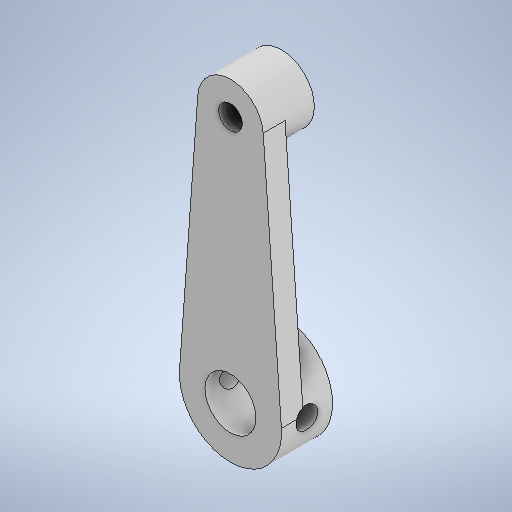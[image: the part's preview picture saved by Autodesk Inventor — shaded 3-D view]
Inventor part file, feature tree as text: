
AUTODESK INVENTOR PART (.ipt)
format: ipt  version: 2025.1 (Build 291241000, 241)  size: 302,080 bytes
history: native  units: mm
features: sketch x4, hole x3, extrude x2, plane x1
ambient origin geometry x8: Origin, YZ Plane, XZ Plane, XY Plane, X Axis, Y Axis, Z Axis, Center Point
bodies: Volumenkörper1 (feature_tree)
feature tree (10):
  extrude  "Extrusion1"  Depth=14.0mm
  extrude  "Extrusion2"  Depth=3.0mm TaperAngle=0.0deg
  sketch  "Skizze3"  dims[d5=9.0mm d6=14.0mm]
  hole  "Bohrung1"  [1 undecoded]
  hole  "Bohrung2"  [1 undecoded]
  plane  "Arbeitsebene1"
  hole  "Bohrung3"  [1 undecoded]
  sketch  "Skizze1"  dims[d0=34.0mm d1=14.0mm]
  sketch  "Skizze2"  dims[d2=9.0mm d3=3.0mm d4=0.0mm]
  sketch  "Skizze4"  dims[d7=4.0mm d8=0.0mm d9=3.242mm d10=8.0mm d11=4.0mm d12=2.0mm d13=90.0deg d14=11.8mm d15=0.0mm d16=7.0mm d17=8.0mm d18=4.0mm d19=2.0mm d20=90.0deg d21=8.0mm d22=0.0mm d23=-7.0mm d24=3.5mm d25=3.0mm d26=6.0mm d27=4.0mm d28=2.0mm d29=90.0deg d30=8.0mm d31=0.0mm]
note: 3 required parameter values undecoded (feature->parameter linkage not recoverable at this tier; creation-order binding heuristic only, values carry confidence <= 0.55)
